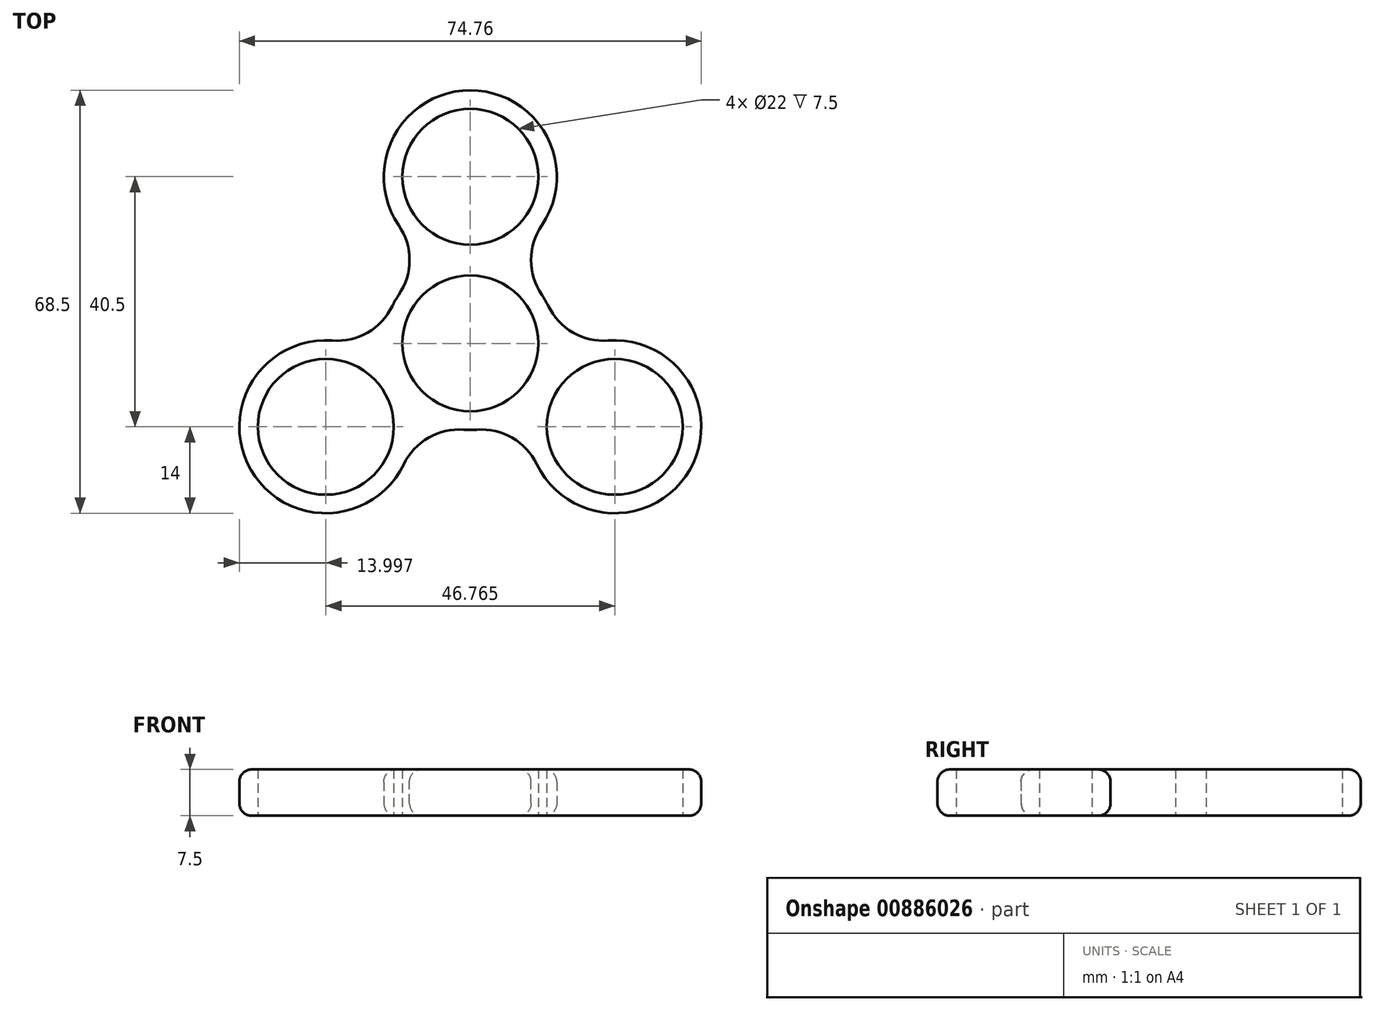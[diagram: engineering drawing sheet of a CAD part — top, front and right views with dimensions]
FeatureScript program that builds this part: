
annotation { "Feature Type Name" : "Feature", "Feature Type Description" : "" }
export const myFeature = defineFeature(function(context is Context, id is Id, definition is map)
    precondition{}
    {
        {
            var Q0;
            Q0=qCreatedBy(makeId("Top.planeOp"),FACE);
            var sketch = newSketch(context, id + "F0", { "sketchPlane" : qUnion([Q0])});
            skCircle(sketch, "E0", {"center": v(0, 0) * mm, "radius": 11 * mm});
            skArc(sketch, "E1", {"start": v(-3.7, 13.5) * mm, "mid": v(-12.12, 7) * mm, "end": v(-13.55, -3.54) * mm});
            skCircle(sketch, "E2", {"center": v(0, 27) * mm, "radius": 11 * mm});
            skArc(sketch, "E3", {"start": v(3.7, 13.5) * mm, "mid": v(0, 41) * mm, "end": v(-3.7, 13.5) * mm});
            skLineSegment(sketch, "E4", {"start": v(0, 0) * mm, "end": v(23.38, -13.5) * mm, "construction": true});
            skCircle(sketch, "E5", {"center": v(23.38, -13.5) * mm, "radius": 11 * mm});
            skArc(sketch, "E6", {"start": v(9.84, -9.96) * mm, "mid": v(35.5, -20.5) * mm, "end": v(13.55, -3.54) * mm});
            skArc(sketch, "E7.MirrorC", {"start": v(-9.84, -9.96) * mm, "mid": v(-35.5, -20.5) * mm, "end": v(-13.55, -3.54) * mm});
            skCircle(sketch, "E8.MirrorC", {"center": v(-23.38, -13.5) * mm, "radius": 11 * mm});
            skArc(sketch, "E9.trimOffspring", {"start": v(-9.84, -9.96) * mm, "mid": v(0, -14) * mm, "end": v(9.84, -9.96) * mm});
            skArc(sketch, "E10.trimOffspring", {"start": v(13.55, -3.54) * mm, "mid": v(12.12, 7) * mm, "end": v(3.7, 13.5) * mm});
            skSolve(sketch);
        }
        {
            var Q0;
            Q0=makeQuery(id+"F0.imprint","IMPRINT",FACE,{"disambiguationData":[TD([[makeQuery(id+"F0.imprint","IMPRINT",EDGE,{"derivedFrom":sQuery(id+"F0.wireOp",EDGE,"E0")}),-1.0]])]});
            extrude(context, id + "F1", {"entities" : qUnion([Q0]), "depth" : 7.5 * mm, "offsetDistance" : 25 * mm});
        }
        {
            var Q0;
            Q0=makeQuery(id+"F1.opExtrude","SWEPT_EDGE",EDGE,{"disambiguationData":[OSD([sQuery(id+"F0.wireOp",EDGE,"E7.MirrorC"),sQuery(id+"F0.wireOp",EDGE,"E9.trimOffspring")])]});
            var Q1;
            Q1=makeQuery(id+"F1.opExtrude","SWEPT_EDGE",EDGE,{"disambiguationData":[OSD([sQuery(id+"F0.wireOp",EDGE,"E6"),sQuery(id+"F0.wireOp",EDGE,"E9.trimOffspring")])]});
            var Q2;
            Q2=makeQuery(id+"F1.opExtrude","SWEPT_EDGE",EDGE,{"disambiguationData":[OSD([sQuery(id+"F0.wireOp",EDGE,"E1"),sQuery(id+"F0.wireOp",EDGE,"E7.MirrorC")])]});
            var Q3;
            Q3=makeQuery(id+"F1.opExtrude","SWEPT_EDGE",EDGE,{"disambiguationData":[OSD([sQuery(id+"F0.wireOp",EDGE,"E1"),sQuery(id+"F0.wireOp",EDGE,"E3")])]});
            var Q4;
            Q4=makeQuery(id+"F1.opExtrude","SWEPT_EDGE",EDGE,{"disambiguationData":[OSD([sQuery(id+"F0.wireOp",EDGE,"E3"),sQuery(id+"F0.wireOp",EDGE,"E10.trimOffspring")])]});
            var Q5;
            Q5=makeQuery(id+"F1.opExtrude","SWEPT_EDGE",EDGE,{"disambiguationData":[OSD([sQuery(id+"F0.wireOp",EDGE,"E6"),sQuery(id+"F0.wireOp",EDGE,"E10.trimOffspring")])]});
            fillet(context, id + "F2", {"entities" : qUnion([Q0, Q1, Q2, Q3, Q4, Q5]), "radius" : 10 * mm, "tangentPropagation" : true, "allowEdgeOverflow" : false});
        }
        {
            var Q0;
            Q0=makeQuery(id+"F1.opExtrude","CAP_EDGE",EDGE,{"disambiguationData":[OSD([sQuery(id+"F0.wireOp",EDGE,"E7.MirrorC")])],"isStart":false});
            var Q1;
            Q1=makeQuery(id+"F1.opExtrude","CAP_EDGE",EDGE,{"disambiguationData":[OSD([sQuery(id+"F0.wireOp",EDGE,"E7.MirrorC")])],"isStart":true});
            fillet(context, id + "F3", {"entities" : qUnion([Q0, Q1]), "radius" : 2 * mm, "tangentPropagation" : true, "allowEdgeOverflow" : false});
        }
    });
